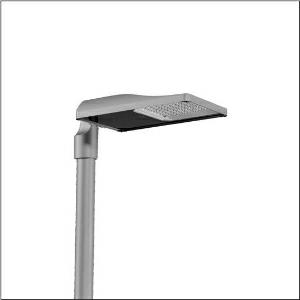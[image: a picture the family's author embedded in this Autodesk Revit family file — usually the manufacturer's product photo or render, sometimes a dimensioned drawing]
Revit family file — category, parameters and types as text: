
# Revit family: streetlight_sl_31_midi___pl52_5xh7h4aa08ma_ed53
name_source: partatom
category: Lighting Fixtures
units: mm (PartAtom-declared; Revit-internal decimal feet)

## family parameters
Cut with Voids When Loaded = No
Host = Face
Light Source = No
Part Type = Normal
Room Calculation Point = No
Round Connector Dimension = Use Diameter
Shared = No

## types (1)
- --- (1 x LED, 19840 lm, 145.3 W, 4000K)
    Apparent Load = 145 VA
    CIE Flux Codes = 27 59 98 100 100
    Color Rendering = 70
    Color Temperature = 4000K
    Default Elevation = 1800 mm
    Description = Streetlight SL 31 midi Easy LST mast luminaire for post-top, side-entry; light control with lens of PMMA; light distribution: PL52, direct asymmetric distribution, for standard-compliant lighting for roads and squares; LED: luminous flux: 19.840lm, light colour: 740, colour temperature: 4000K; luminous efficacy: 136,5lm/W; control: pre-setting: linear dimming characteristic, flexible luminous flux parameterisation, time-dependent luminous flux control, constant luminous flux control, power reduction, intelligent temperature release in ECG and LED module, overheat protection; luminaire housing, of diecast aluminium, Siteco® metallic grey (DB 702S), corrosivity category C5 high according to DIN EN ISO 12944; cover of toughened safety glass, transparent, opened without tools; mast flange of diecast aluminium, Siteco® metallic grey (DB 702S), spigot size: 76/60mm, mast flange included unmounted; with cable H07RN-F 3x 1.5mm², cable length: 10,5m, connection cable pre-assembled; mains connection: 220..240V, AC, 50/60Hz; power consumption (at start of service life): 145,3W / (at end of service life): 161,8W / (with reduced operation 50%): 61,1W; protection rating (complete): IP66; insulation class (complete): insulation class II (safety insulation); impact resistance: IK10; certification: CE, ENEC, ENEC+, VDE, UKCA; permissible operating ambient temperature for outdoor applications: -40..+50°C; packaging unit: 1 piece

Light Distribution: PL52
    Height = 79 mm
    Lamp = 1 x LED
    Lamp Light Flux = 19840 lm
    Lamp Power = 145.3 W
    Lamp count = 1
    Length = 577 mm
    Luminous efficacy = 137 lm/W
    Manufacturer = Siteco
    ModVariant = No
    Model = 5XH7H4AA08MA
    Number of Poles = 1
    OnlyDefault = Yes
    Power Factor = 1
    Product Name = Streetlight SL 31 midi | PL52
    Product group = mast luminaire | pylon top
    ProductGroupID = 6100
    Protection Class = Protection class II
    Protection Degree = IP 66
    RLX_Detail_Level = 1
    RLX_Emergency_Light_Flux = 0 lm
    RLX_Emergency_Type = 0
    RLX_Emergency_Type_DB = No
    RlxData = <blob elided: 52449 chars, md5=9169609e>
    Socket = socket
    Standby Power = 0 W
    System Light Flux = 19841 lm
    System Power = 145 W
    Type Comments = factory setting: luminous flux: 100 % | dim-lin: 254 | 747 mA
    Type Image = l_1300317.jpg
    URL = http://relux.com
    VarID = @adj_057794
    Voltage = 0 V
    Weight = 0.00 kg
    Width = 362 mm

## geometry (parser evidence)
native form markers: Blend x4, Sweep x11
no freeform markers — native parametric forms only
